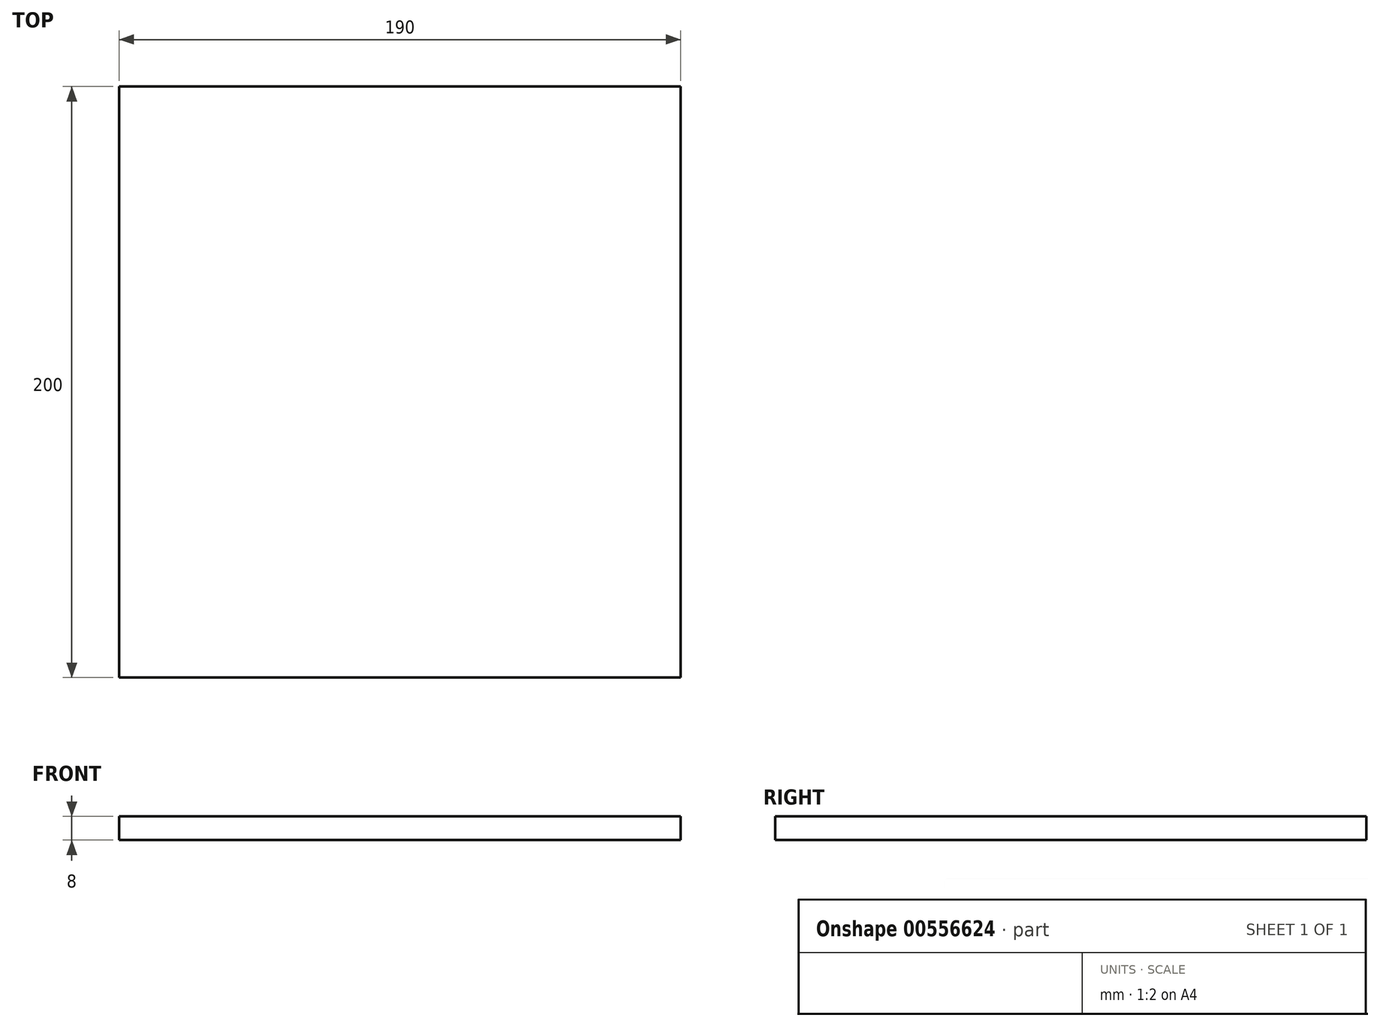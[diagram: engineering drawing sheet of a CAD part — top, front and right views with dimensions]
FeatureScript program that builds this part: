
annotation { "Feature Type Name" : "Feature", "Feature Type Description" : "" }
export const myFeature = defineFeature(function(context is Context, id is Id, definition is map)
    precondition{}
    {
        {
            var Q0;
            Q0=qCreatedBy(makeId("Top.planeOp"),FACE);
            var sketch = newSketch(context, id + "F0", { "sketchPlane" : qUnion([Q0])});
            skLineSegment(sketch, "E0", {"start": v(0, -74.94) * mm, "end": v(0, 125.06) * mm});
            skLineSegment(sketch, "E1", {"start": v(0, 125.06) * mm, "end": v(190, 125.06) * mm});
            skLineSegment(sketch, "E2", {"start": v(190, 125.06) * mm, "end": v(190, -74.94) * mm});
            skLineSegment(sketch, "E3", {"start": v(190, -74.94) * mm, "end": v(0, -74.94) * mm});
            skSolve(sketch);
        }
        {
            var Q0;
            Q0=makeQuery(id+"F0.imprint","IMPRINT",FACE,{"disambiguationData":[TD([[makeQuery(id+"F0.imprint","IMPRINT",EDGE,{"derivedFrom":sQuery(id+"F0.wireOp",EDGE,"E0")}),-1.0]])]});
            extrude(context, id + "F1", {"entities" : qUnion([Q0]), "endBound" : BoundingType.SYMMETRIC, "depth" : 8 * mm, "offsetDistance" : 25 * mm});
        }
    });
